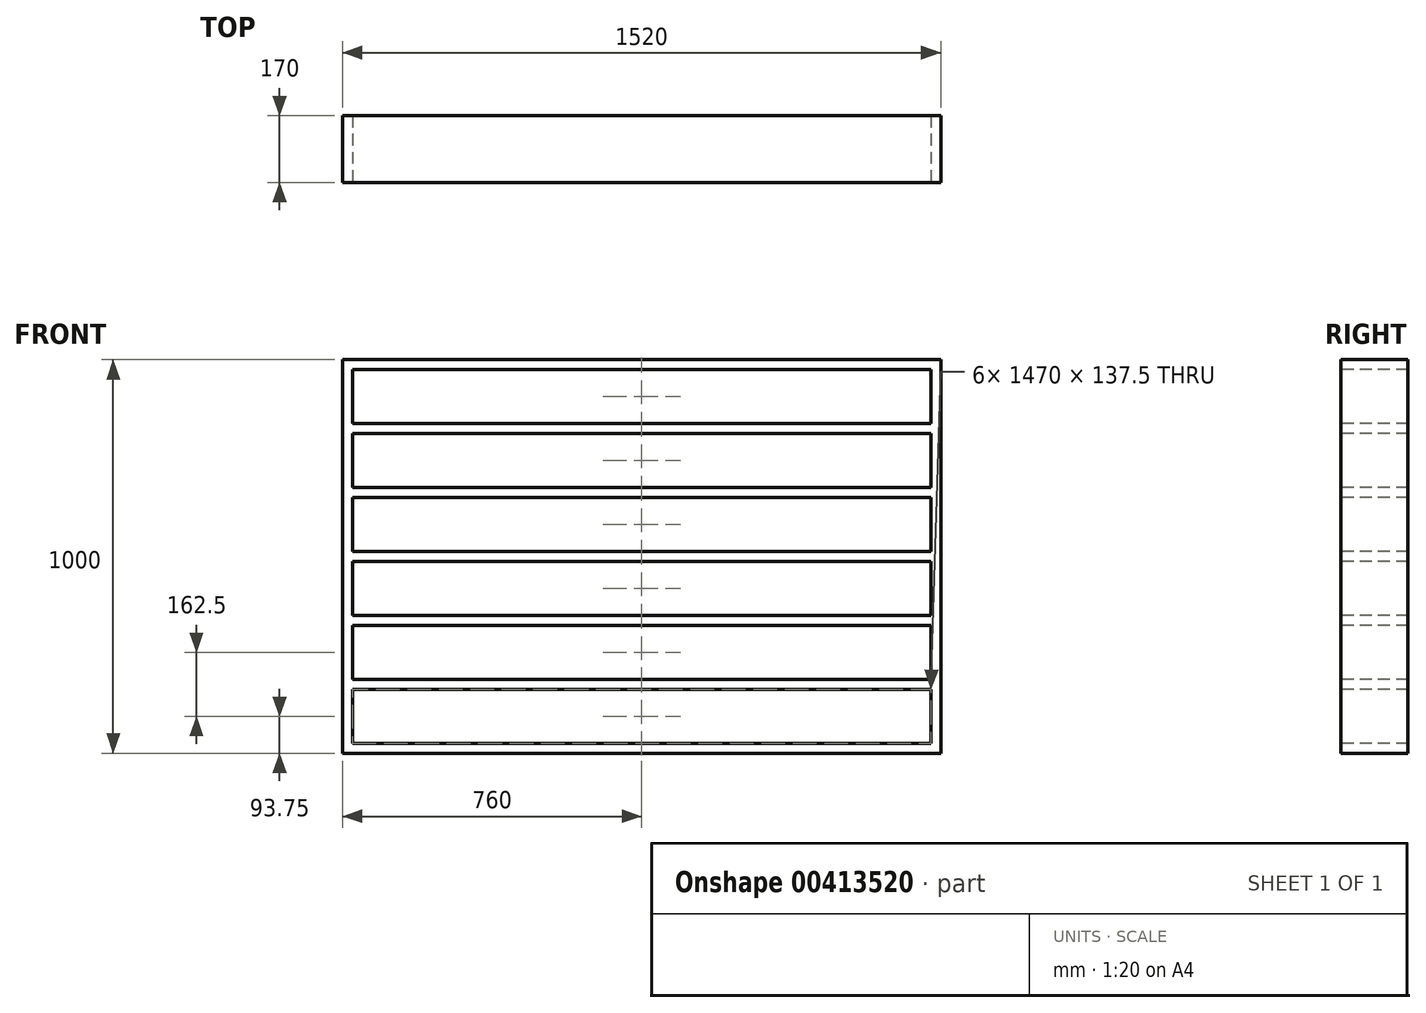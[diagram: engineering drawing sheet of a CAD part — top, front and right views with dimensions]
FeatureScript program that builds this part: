
annotation { "Feature Type Name" : "Feature", "Feature Type Description" : "" }
export const myFeature = defineFeature(function(context is Context, id is Id, definition is map)
    precondition{}
    {
        {
            var Q0;
            Q0=qCreatedBy(makeId("Front.planeOp"),FACE);
            var sketch = newSketch(context, id + "F0", { "sketchPlane" : qUnion([Q0])});
            skLineSegment(sketch, "E0.bottom", {"start": v(760, 500) * mm, "end": v(-760, 500) * mm});
            skLineSegment(sketch, "E0.top", {"start": v(760, -500) * mm, "end": v(-760, -500) * mm});
            skLineSegment(sketch, "E0.left", {"start": v(760, 500) * mm, "end": v(760, -500) * mm});
            skLineSegment(sketch, "E0.right", {"start": v(-760, 500) * mm, "end": v(-760, -500) * mm});
            skPoint(sketch, "E0.middle", {"position": v(0, 0) * mm});
            skSolve(sketch);
        }
        {
            var Q0;
            Q0=makeQuery(id+"F0.imprint","IMPRINT",FACE,{"disambiguationData":[TD([[makeQuery(id+"F0.imprint","IMPRINT",EDGE,{"derivedFrom":sQuery(id+"F0.wireOp",EDGE,"E0.bottom")}),1.0]])]});
            extrude(context, id + "F1", {"entities" : qUnion([Q0]), "oppositeDirection" : true, "offsetDistance" : 25 * mm, "depth" : 170 * mm});
        }
        {
            var Q0;
            Q0=makeQuery(id+"F1.opExtrude","CAP_FACE",FACE,{"disambiguationData":[OSD([sQuery(id+"F0.wireOp",EDGE,"E0.bottom"),sQuery(id+"F0.wireOp",EDGE,"E0.top"),sQuery(id+"F0.wireOp",EDGE,"E0.left"),sQuery(id+"F0.wireOp",EDGE,"E0.right")])],"isStart":true});
            var sketch = newSketch(context, id + "F2", { "sketchPlane" : qUnion([Q0])});
            skLineSegment(sketch, "E1.bottom", {"start": v(-735, -475) * mm, "end": v(735, -475) * mm});
            skLineSegment(sketch, "E1.left", {"start": v(-735, -475) * mm, "end": v(-735, -337.5) * mm});
            skLineSegment(sketch, "E1.right", {"start": v(735, -475) * mm, "end": v(735, -425) * mm});
            skPoint(sketch, "E2.middle", {"position": v(0, 0) * mm});
            skLineSegment(sketch, "E3", {"start": v(-735, -312.5) * mm, "end": v(-735, -175) * mm});
            skLineSegment(sketch, "E4", {"start": v(-735, 475) * mm, "end": v(735, 475) * mm});
            skLineSegment(sketch, "E5", {"start": v(735, 475) * mm, "end": v(735, 337.5) * mm});
            skLineSegment(sketch, "E6", {"start": v(-735, 0) * mm, "end": v(735, 0) * mm, "construction": true});
            skLineSegment(sketch, "E7", {"start": v(-735, -337.5) * mm, "end": v(735, -337.5) * mm});
            skLineSegment(sketch, "E8", {"start": v(-735, -312.5) * mm, "end": v(735, -312.5) * mm});
            skLineSegment(sketch, "E9", {"start": v(-735, -175) * mm, "end": v(735, -175) * mm});
            skLineSegment(sketch, "E10", {"start": v(-735, -150) * mm, "end": v(735, -150) * mm});
            skLineSegment(sketch, "E11", {"start": v(-735, -12.5) * mm, "end": v(735, -12.5) * mm});
            skLineSegment(sketch, "E12", {"start": v(-735, 12.5) * mm, "end": v(735, 12.5) * mm});
            skLineSegment(sketch, "E13.MirrorCS", {"start": v(-735, 337.5) * mm, "end": v(735, 337.5) * mm});
            skLineSegment(sketch, "E14.MirrorCS", {"start": v(-735, 312.5) * mm, "end": v(735, 312.5) * mm});
            skLineSegment(sketch, "E15.MirrorCS", {"start": v(-735, 150) * mm, "end": v(735, 150) * mm});
            skLineSegment(sketch, "E16.MirrorCS", {"start": v(-735, 175) * mm, "end": v(735, 175) * mm});
            skLineSegment(sketch, "E17.trimOffspring", {"start": v(735, 312.5) * mm, "end": v(735, 175) * mm});
            skLineSegment(sketch, "E18.trimOffspring", {"start": v(-735, 337.5) * mm, "end": v(-735, 475) * mm});
            skLineSegment(sketch, "E19.trimOffspring", {"start": v(-735, 175) * mm, "end": v(-735, 312.5) * mm});
            skLineSegment(sketch, "E20.trimOffspring", {"start": v(-735, 12.5) * mm, "end": v(-735, 150) * mm});
            skLineSegment(sketch, "E21.trimOffspring", {"start": v(-735, -150) * mm, "end": v(-735, -12.5) * mm});
            skLineSegment(sketch, "E22.trimOffspring", {"start": v(735, -337.5) * mm, "end": v(735, -425) * mm});
            skLineSegment(sketch, "E23.trimOffspring", {"start": v(735, -175) * mm, "end": v(735, -312.5) * mm});
            skLineSegment(sketch, "E24.trimOffspring", {"start": v(735, 150) * mm, "end": v(735, 12.5) * mm});
            skLineSegment(sketch, "E25.trimOffspring", {"start": v(735, -12.5) * mm, "end": v(735, -150) * mm});
            skSolve(sketch);
        }
        {
            var Q0;
            Q0=makeQuery(id+"F2.imprint","IMPRINT",FACE,{"disambiguationData":[TD([[makeQuery(id+"F2.imprint","IMPRINT",EDGE,{"derivedFrom":sQuery(id+"F2.wireOp",EDGE,"E4")}),-1.0]])]});
            var Q1;
            Q1=makeQuery(id+"F2.imprint","IMPRINT",FACE,{"disambiguationData":[TD([[makeQuery(id+"F2.imprint","IMPRINT",EDGE,{"derivedFrom":sQuery(id+"F2.wireOp",EDGE,"E14.MirrorCS")}),-1.0]])]});
            var Q2;
            Q2=makeQuery(id+"F2.imprint","IMPRINT",FACE,{"disambiguationData":[TD([[makeQuery(id+"F2.imprint","IMPRINT",EDGE,{"derivedFrom":sQuery(id+"F2.wireOp",EDGE,"E12")}),1.0]])]});
            var Q3;
            Q3=makeQuery(id+"F2.imprint","IMPRINT",FACE,{"disambiguationData":[TD([[makeQuery(id+"F2.imprint","IMPRINT",EDGE,{"derivedFrom":sQuery(id+"F2.wireOp",EDGE,"E10")}),1.0]])]});
            var Q4;
            Q4=makeQuery(id+"F2.imprint","IMPRINT",FACE,{"disambiguationData":[TD([[makeQuery(id+"F2.imprint","IMPRINT",EDGE,{"derivedFrom":sQuery(id+"F2.wireOp",EDGE,"E3")}),-1.0]])]});
            var Q5;
            Q5=makeQuery(id+"F2.imprint","IMPRINT",FACE,{"disambiguationData":[TD([[makeQuery(id+"F2.imprint","IMPRINT",EDGE,{"derivedFrom":sQuery(id+"F2.wireOp",EDGE,"E1.bottom")}),1.0]])]});
            var Q6;
            Q6=makeQuery(id+"F1.opExtrude","CAP_FACE",FACE,{"disambiguationData":[OSD([sQuery(id+"F0.wireOp",EDGE,"E0.bottom"),sQuery(id+"F0.wireOp",EDGE,"E0.top"),sQuery(id+"F0.wireOp",EDGE,"E0.left"),sQuery(id+"F0.wireOp",EDGE,"E0.right")])],"isStart":false});
            extrude(context, id + "F3", {"entities" : qUnion([Q0, Q1, Q2, Q3, Q4, Q5]), "operationType" : NewBodyOperationType.REMOVE, "endBound" : BoundingType.UP_TO_SURFACE, "oppositeDirection" : true, "depth" : 25 * mm, "endBoundEntityFace" : qUnion([Q6]), "offsetDistance" : 25 * mm});
        }
    });
